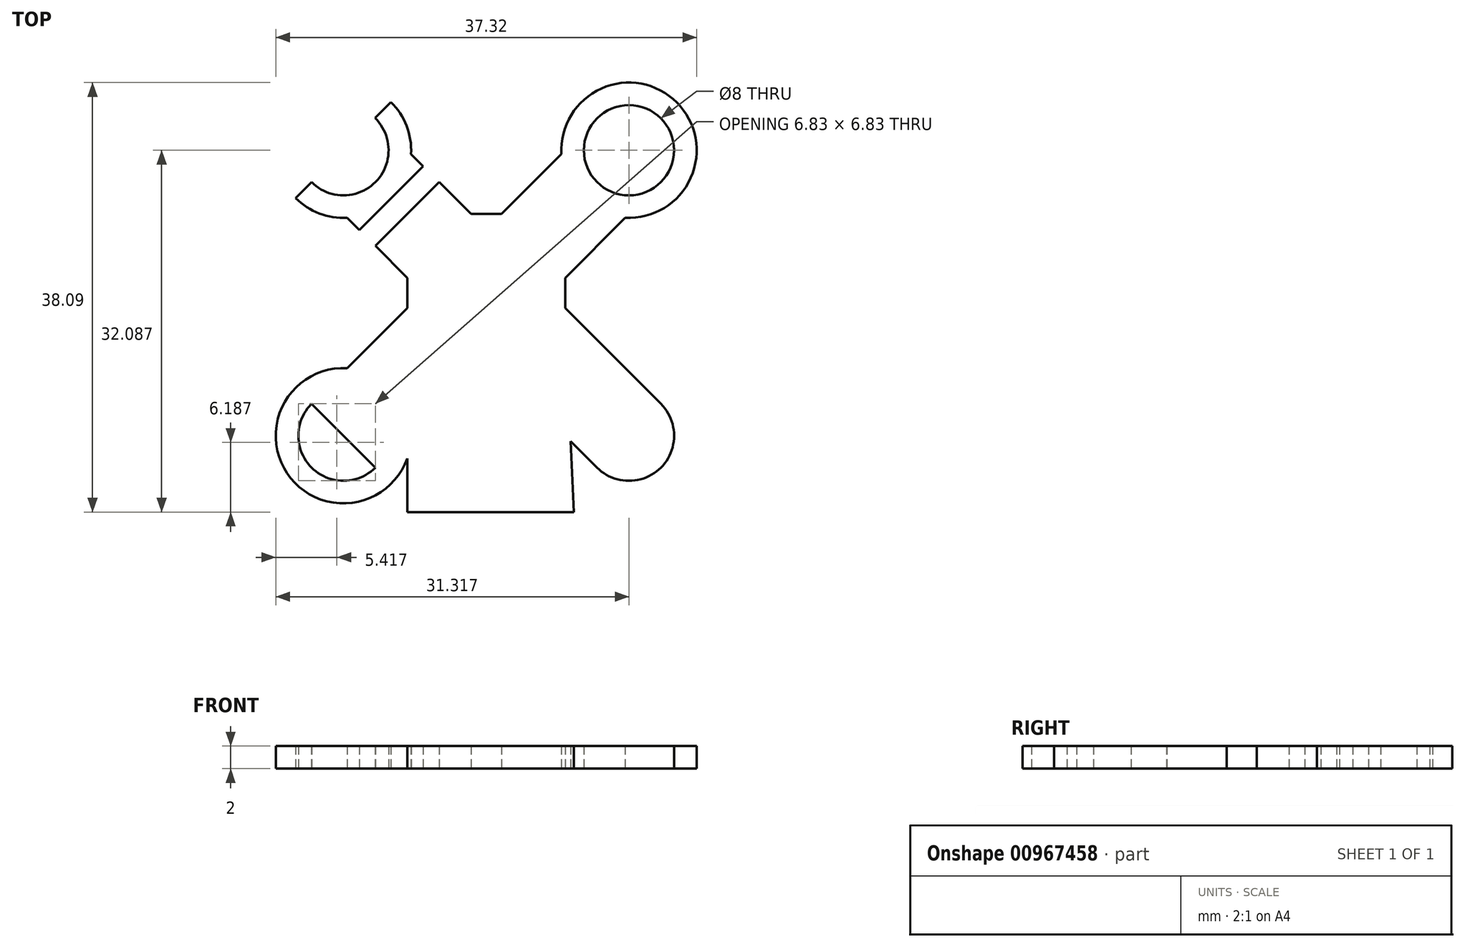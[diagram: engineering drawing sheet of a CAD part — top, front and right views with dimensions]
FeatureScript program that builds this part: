
annotation { "Feature Type Name" : "Feature", "Feature Type Description" : "" }
export const myFeature = defineFeature(function(context is Context, id is Id, definition is map)
    precondition{}
    {
        {
            var Q0;
            Q0=qCreatedBy(makeId("Top.planeOp"),FACE);
            var sketch = newSketch(context, id + "F0", { "sketchPlane" : qUnion([Q0])});
            skLineSegment(sketch, "E0.bottom", {"start": v(-1.34, 7) * mm, "end": v(1.34, 7) * mm});
            skLineSegment(sketch, "E0.top", {"start": v(-1.34, -7) * mm, "end": v(1.34, -7) * mm});
            skLineSegment(sketch, "E0.left", {"start": v(-7, 1.34) * mm, "end": v(-7, -1.34) * mm});
            skLineSegment(sketch, "E0.right", {"start": v(7, 1.34) * mm, "end": v(7, -1.34) * mm});
            skLineSegment(sketch, "E1", {"start": v(-18.48, 18.48) * mm, "end": v(18.48, -18.48) * mm, "construction": true});
            skLineSegment(sketch, "E2", {"start": v(-18.48, -18.48) * mm, "end": v(18.48, 18.48) * mm, "construction": true});
            skLineSegment(sketch, "E3", {"start": v(-6.67, 12.32) * mm, "end": v(-5.59, 11.24) * mm});
            skLineSegment(sketch, "E4", {"start": v(15.49, -9.83) * mm, "end": v(9.83, -15.49) * mm});
            skLineSegment(sketch, "E5", {"start": v(9.83, -15.49) * mm, "end": v(1.34, -7) * mm});
            skLineSegment(sketch, "E6", {"start": v(-15.49, -9.83) * mm, "end": v(-9.83, -15.49) * mm});
            skLineSegment(sketch, "E7", {"start": v(-9.83, -15.49) * mm, "end": v(-1.34, -7) * mm});
            skLineSegment(sketch, "E8", {"start": v(15.49, 9.83) * mm, "end": v(9.83, 15.49) * mm});
            skLineSegment(sketch, "E9", {"start": v(9.83, 15.49) * mm, "end": v(1.34, 7) * mm});
            skArc(sketch, "E10", {"start": v(-15.49, 9.83) * mm, "mid": v(-9.82, 9.84) * mm, "end": v(-9.85, 15.5) * mm});
            skCircle(sketch, "E11", {"center": v(12.66, 12.66) * mm, "radius": 4 * mm});
            skCircle(sketch, "E12", {"center": v(12.66, -12.66) * mm, "radius": 4 * mm});
            skArc(sketch, "E13", {"start": v(-15.49, -9.83) * mm, "mid": v(-12.66, -16.66) * mm, "end": v(-9.83, -9.83) * mm});
            skArc(sketch, "E14.0", {"start": v(-16.9, 8.4) * mm, "mid": v(-14.8, 7.05) * mm, "end": v(-12.32, 6.67) * mm});
            skLineSegment(sketch, "E15", {"start": v(-11.24, 5.59) * mm, "end": v(-5.59, 11.24) * mm});
            skLineSegment(sketch, "E16", {"start": v(-4.17, 9.83) * mm, "end": v(-9.83, 4.17) * mm});
            skCircle(sketch, "E17.0", {"center": v(12.66, 12.66) * mm, "radius": 6 * mm});
            skArc(sketch, "E18.0", {"start": v(-12.32, -6.67) * mm, "mid": v(-16.9, -16.9) * mm, "end": v(-6.67, -12.32) * mm});
            skLineSegment(sketch, "E19", {"start": v(-16.9, 8.4) * mm, "end": v(-15.48, 9.83) * mm});
            skLineSegment(sketch, "E20.trimOffspring", {"start": v(-15.48, 9.83) * mm, "end": v(-15.49, 9.83) * mm});
            skPoint(sketch, "E21.orphan", {"position": v(-9.83, 15.49) * mm});
            skArc(sketch, "E22.trimOffspring", {"start": v(-6.67, 12.32) * mm, "mid": v(-7.06, 14.82) * mm, "end": v(-8.45, 16.93) * mm});
            skLineSegment(sketch, "E23.trimOffspring", {"start": v(-11.24, 5.59) * mm, "end": v(-12.32, 6.67) * mm});
            skLineSegment(sketch, "E24.trimOffspring", {"start": v(-4.17, 9.83) * mm, "end": v(-1.34, 7) * mm});
            skLineSegment(sketch, "E25.trimOffspring", {"start": v(-9.85, 15.5) * mm, "end": v(-8.45, 16.93) * mm});
            skLineSegment(sketch, "E26.trimOffspring", {"start": v(-7, -1.34) * mm, "end": v(-15.49, -9.83) * mm});
            skLineSegment(sketch, "E27.trimOffspring", {"start": v(-7, 1.34) * mm, "end": v(-9.83, 4.17) * mm});
            skLineSegment(sketch, "E28.trimOffspring", {"start": v(7, 1.34) * mm, "end": v(15.49, 9.83) * mm});
            skLineSegment(sketch, "E29.trimOffspring", {"start": v(7, -1.34) * mm, "end": v(15.49, -9.83) * mm});
            skLineSegment(sketch, "E30", {"start": v(-7, -1.34) * mm, "end": v(-7, -19.43) * mm});
            skLineSegment(sketch, "E31", {"start": v(-7, -19.43) * mm, "end": v(7.76, -19.43) * mm});
            skLineSegment(sketch, "E32", {"start": v(7.76, -19.43) * mm, "end": v(7, -1.34) * mm});
            skSolve(sketch);
        }
        {
            var Q0;
            Q0 = qSketchRegion(id + "F0", true);
            extrude(context, id + "F1", {"entities" : qUnion([Q0]), "endBound" : BoundingType.SYMMETRIC, "depth" : 2 * mm, "offsetDistance" : 25 * mm});
        }
    });
